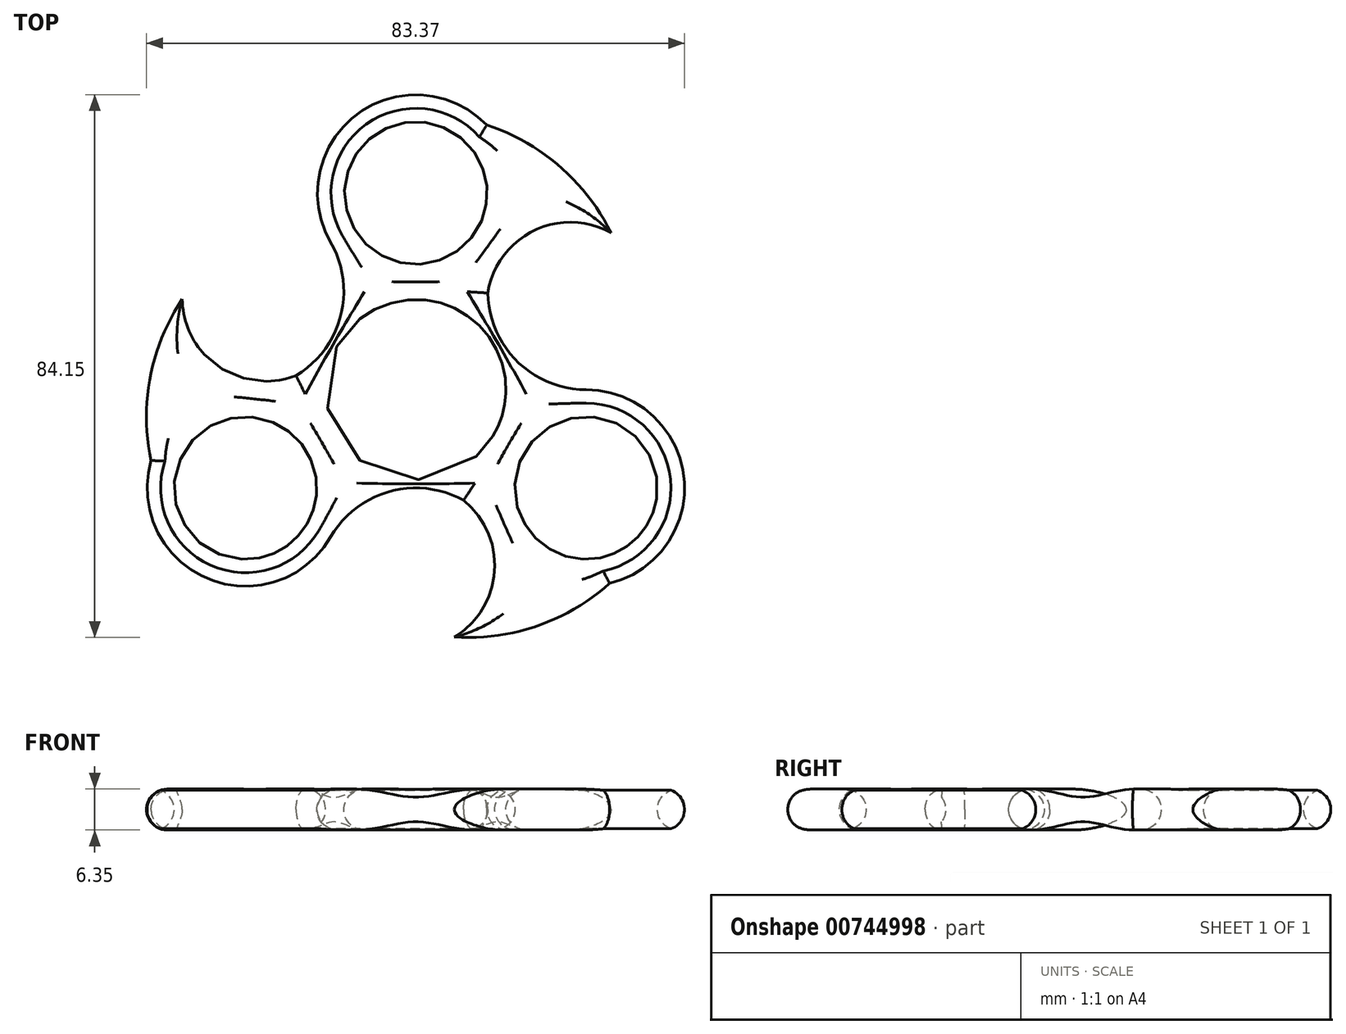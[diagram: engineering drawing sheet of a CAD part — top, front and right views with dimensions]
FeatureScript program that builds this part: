
annotation { "Feature Type Name" : "Feature", "Feature Type Description" : "" }
export const myFeature = defineFeature(function(context is Context, id is Id, definition is map)
    precondition{}
    {
        {
            var Q0;
            Q0=qCreatedBy(makeId("Top.planeOp"),FACE);
            var sketch = newSketch(context, id + "F0", { "sketchPlane" : qUnion([Q0])});
            skCircle(sketch, "E0", {"center": v(0, 0) * mm, "radius": 11.05 * mm});
            skCircle(sketch, "E1", {"center": v(0, 0) * mm, "radius": 13.97 * mm});
            skCircle(sketch, "E2", {"center": v(0, 30.48) * mm, "radius": 11.05 * mm});
            skArc(sketch, "E3", {"start": v(11, 41.03) * mm, "mid": v(-9.15, 42.67) * mm, "end": v(-13.2, 22.86) * mm});
            skCircle(sketch, "E4.1.0", {"center": v(-26.4, -15.24) * mm, "radius": 11.05 * mm});
            skArc(sketch, "E4.1.1", {"start": v(-41.03, -10.99) * mm, "mid": v(-32.38, -29.26) * mm, "end": v(-13.2, -22.86) * mm});
            skCircle(sketch, "E4.2.0", {"center": v(26.4, -15.24) * mm, "radius": 11.05 * mm});
            skArc(sketch, "E4.2.1", {"start": v(30.03, -30.04) * mm, "mid": v(41.53, -13.41) * mm, "end": v(26.4, 0) * mm});
            skArc(sketch, "E5", {"start": v(-18.55, 2.17) * mm, "mid": v(-11.64, 11.42) * mm, "end": v(-13.2, 22.86) * mm});
            skArc(sketch, "E6.1.0", {"start": v(7.4, -17.15) * mm, "mid": v(-4.07, -15.8) * mm, "end": v(-13.2, -22.86) * mm});
            skArc(sketch, "E6.2.0", {"start": v(11.16, 14.98) * mm, "mid": v(15.71, 4.37) * mm, "end": v(26.4, 0) * mm});
            skArc(sketch, "E7", {"start": v(30.24, 24.34) * mm, "mid": v(22.3, 34.62) * mm, "end": v(11, 41.03) * mm});
            skArc(sketch, "E8", {"start": v(30.24, 24.34) * mm, "mid": v(18.26, 24.64) * mm, "end": v(11.16, 14.98) * mm});
            skArc(sketch, "E9.1.0", {"start": v(-36.2, 14.01) * mm, "mid": v(-41.14, 2) * mm, "end": v(-41.03, -10.99) * mm});
            skArc(sketch, "E9.1.1", {"start": v(-36.2, 14.01) * mm, "mid": v(-30.46, 3.5) * mm, "end": v(-18.55, 2.17) * mm});
            skArc(sketch, "E9.2.0", {"start": v(5.96, -38.36) * mm, "mid": v(18.84, -36.62) * mm, "end": v(30.03, -30.04) * mm});
            skArc(sketch, "E9.2.1", {"start": v(5.96, -38.36) * mm, "mid": v(12.2, -28.13) * mm, "end": v(7.4, -17.15) * mm});
            skPoint(sketch, "E10.orphan", {"position": v(13.2, 22.86) * mm});
            skPoint(sketch, "E11.orphan", {"position": v(13.2, -22.86) * mm});
            skPoint(sketch, "E12.orphan", {"position": v(-26.4, 0) * mm});
            skSolve(sketch);
        }
        {
            var Q0;
            Q0=qSketchRegion(id+"F0",true);
            extrude(context, id + "F1", {"entities" : qUnion([Q0]), "depth" : 6.35 * mm, "offsetDistance" : 25.4 * mm});
        }
        {
            var Q0;
            Q0=makeQuery(id+"F1.opExtrude","CAP_FACE",FACE,{"disambiguationData":[OSD([sQuery(id+"F0.wireOp",EDGE,"E1"),sQuery(id+"F0.wireOp",EDGE,"E2"),sQuery(id+"F0.wireOp",EDGE,"E3"),sQuery(id+"F0.wireOp",EDGE,"E4.1.0"),sQuery(id+"F0.wireOp",EDGE,"E4.1.1"),sQuery(id+"F0.wireOp",EDGE,"E4.2.0"),sQuery(id+"F0.wireOp",EDGE,"E4.2.1"),sQuery(id+"F0.wireOp",EDGE,"E5"),sQuery(id+"F0.wireOp",EDGE,"E6.1.0"),sQuery(id+"F0.wireOp",EDGE,"E6.2.0")])],"isStart":false});
            var Q1;
            Q1=makeQuery(id+"F1.opExtrude","CAP_FACE",FACE,{"disambiguationData":[OSD([sQuery(id+"F0.wireOp",EDGE,"E1"),sQuery(id+"F0.wireOp",EDGE,"E2"),sQuery(id+"F0.wireOp",EDGE,"E3"),sQuery(id+"F0.wireOp",EDGE,"E4.1.0"),sQuery(id+"F0.wireOp",EDGE,"E4.1.1"),sQuery(id+"F0.wireOp",EDGE,"E4.2.0"),sQuery(id+"F0.wireOp",EDGE,"E4.2.1"),sQuery(id+"F0.wireOp",EDGE,"E5"),sQuery(id+"F0.wireOp",EDGE,"E6.1.0"),sQuery(id+"F0.wireOp",EDGE,"E6.2.0")])],"isStart":true});
            fillet(context, id + "F2", {"entities" : qUnion([Q0, Q1]), "radius" : 3.17 * mm, "tangentPropagation" : true, "allowEdgeOverflow" : false});
        }
    });
